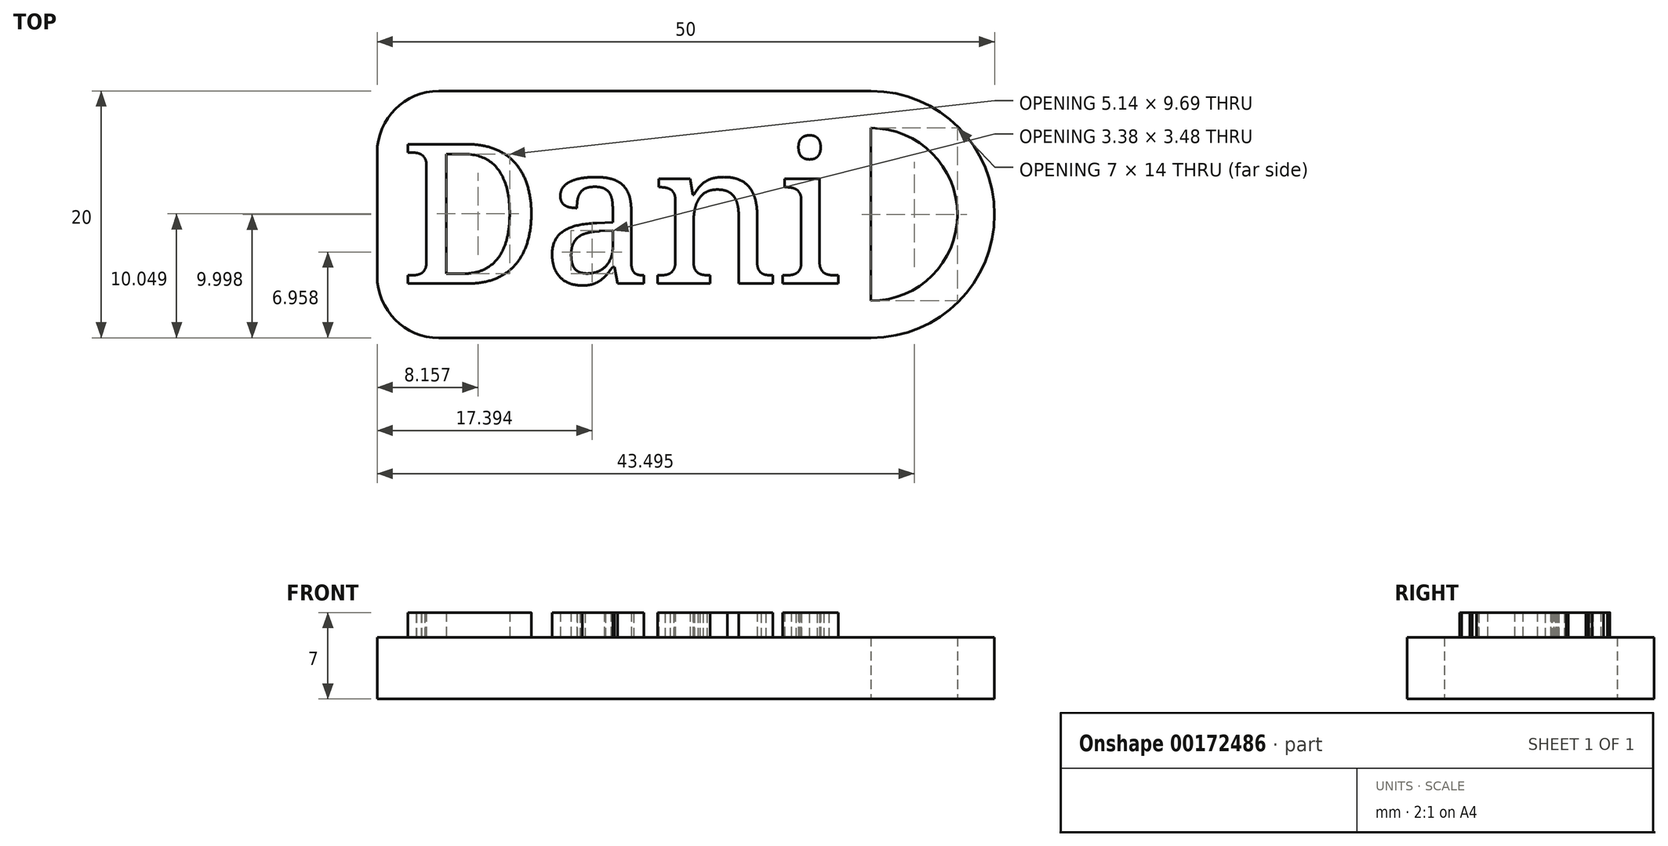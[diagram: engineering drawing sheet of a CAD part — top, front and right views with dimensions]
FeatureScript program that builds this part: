
annotation { "Feature Type Name" : "Feature", "Feature Type Description" : "" }
export const myFeature = defineFeature(function(context is Context, id is Id, definition is map)
    precondition{}
    {
        {
            var Q0;
            Q0=qCreatedBy(makeId("Top.planeOp"),FACE);
            var sketch = newSketch(context, id + "F0", { "sketchPlane" : qUnion([Q0])});
            skLineSegment(sketch, "E0.bottom", {"start": v(-24.2, 14.9) * mm, "end": v(10.8, 14.9) * mm});
            skLineSegment(sketch, "E0.top", {"start": v(-24.2, -5.1) * mm, "end": v(10.8, -5.1) * mm});
            skLineSegment(sketch, "E0.left", {"start": v(-29.2, 9.9) * mm, "end": v(-29.2, -0.1) * mm});
            skLineSegment(sketch, "E0.right", {"start": v(10.8, 14.9) * mm, "end": v(10.8, -5.1) * mm});
            skArc(sketch, "E1", {"start": v(10.8, -5.1) * mm, "mid": v(20.8, 4.9) * mm, "end": v(10.8, 14.9) * mm});
            skArc(sketch, "E2", {"start": v(10.8, -2.1) * mm, "mid": v(17.8, 4.9) * mm, "end": v(10.8, 11.9) * mm});
            skPoint(sketch, "E3.visualSharp", {"position": v(-29.2, 14.9) * mm});
            skArc(sketch, "E3.filletArc", {"start": v(-24.2, 14.9) * mm, "mid": v(-27.74, 13.43) * mm, "end": v(-29.2, 9.9) * mm});
            skPoint(sketch, "E4.visualSharp", {"position": v(-29.2, -5.1) * mm});
            skArc(sketch, "E4.filletArc", {"start": v(-29.2, -0.1) * mm, "mid": v(-27.74, -3.64) * mm, "end": v(-24.2, -5.1) * mm});
            skSolve(sketch);
        }
        {
            var Q0;
            {var subQ2=sQuery(id+"F0.wireOp",EDGE,"E0.bottom");Q0=makeQuery(id+"F0.imprint","IMPRINT",FACE,{"disambiguationData":[TD([[makeQuery(id+"F0.imprint","IMPRINT",EDGE,{"derivedFrom":subQ2}),-1.0]])]});}
            var Q1;
            {var subQ0=sQuery(id+"F0.wireOp",EDGE,"E1");Q1=makeQuery(id+"F0.imprint","IMPRINT",FACE,{"disambiguationData":[TD([[makeQuery(id+"F0.imprint","IMPRINT",EDGE,{"derivedFrom":subQ0}),1.0]])]});}
            extrude(context, id + "F1", {"entities" : qUnion([Q0, Q1]), "depth" : 5 * mm});
        }
        {
            var Q0;
            Q0=makeQuery(id+"F1.opExtrude","CAP_FACE",FACE,{"disambiguationData":[OSD([sQuery(id+"F0.wireOp",EDGE,"E0.bottom"),sQuery(id+"F0.wireOp",EDGE,"E0.top"),sQuery(id+"F0.wireOp",EDGE,"E0.left"),sQuery(id+"F0.wireOp",EDGE,"E0.right"),sQuery(id+"F0.wireOp",EDGE,"E1"),sQuery(id+"F0.wireOp",EDGE,"E2"),sQuery(id+"F0.wireOp",EDGE,"E3.filletArc"),sQuery(id+"F0.wireOp",EDGE,"E4.filletArc")])],"isStart":false});
            var sketch = newSketch(context, id + "F2", { "sketchPlane" : qUnion([Q0])});
            skText(sketch, "E5", { "text": "Dani", "fontName": "NotoSerif-Regular.ttf"});
            const initialGuessF2  = {"E5": [-0.02731, -0.0007, 1, 0, 0.01138]};
            skSetInitialGuess(sketch, initialGuessF2);
            skSolve(sketch);
        }
        {
            var Q0;
            Q0 = qSketchRegion(id + "F2", true);
            extrude(context, id + "F3", {"entities" : qUnion([Q0]), "depth" : 2 * mm});
        }
    });
